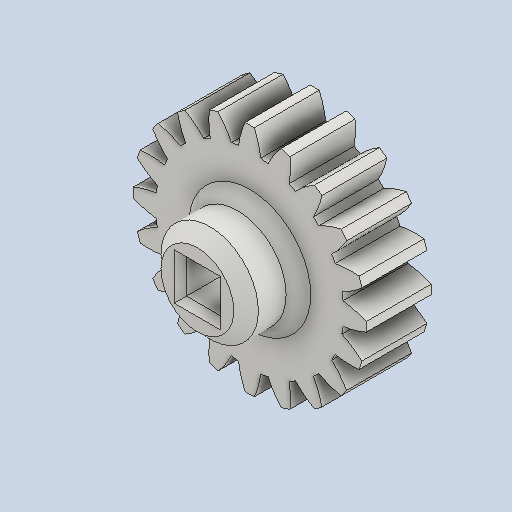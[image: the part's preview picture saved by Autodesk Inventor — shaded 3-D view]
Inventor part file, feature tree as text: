
AUTODESK INVENTOR PART (.ipt)
format: ipt  version: 2022 (Build 260153000, 153)  size: 298,496 bytes
history: native  units: in
note: dims shown in document units (in); Inventor stores cm internally (conversion verified against a paired STEP export)
features: other x12, sketch x4, plane x3
ambient origin geometry x8: Origin, YZ Plane, XZ Plane, XY Plane, X Axis, Y Axis, Z Axis, Center Point
bodies: Solid1 (feature_tree)
feature tree (19):
  other  "Spur Gear2"
  other  "Solid1::Spur Gear2"
  other  "TaggingFeature1"
  sketch  "Sketch1"  dims[d0=0.3937in]
  sketch  "Sketch2"  dims[d9=0.0in d14=0.0in d15=1.0in d16=0.0in d17=0.0in d18=0.0in d19=1.0in]
  sketch  "Sketch3"
  sketch  "Sketch4"
  plane  "XZ Plane_1"
  plane  "Work Plane2"
  plane  "Work Plane3"
  other  "Srf1"
  other  "Srf1::Derived"
  other  "Start plane iMate"
  other  "Distance iMate"
  other  "Position iMate"
  other  "Mesh iMate"
  other  "Axis iMate"
  other  "Mesh iMate2"
  other  "Align iMate"
